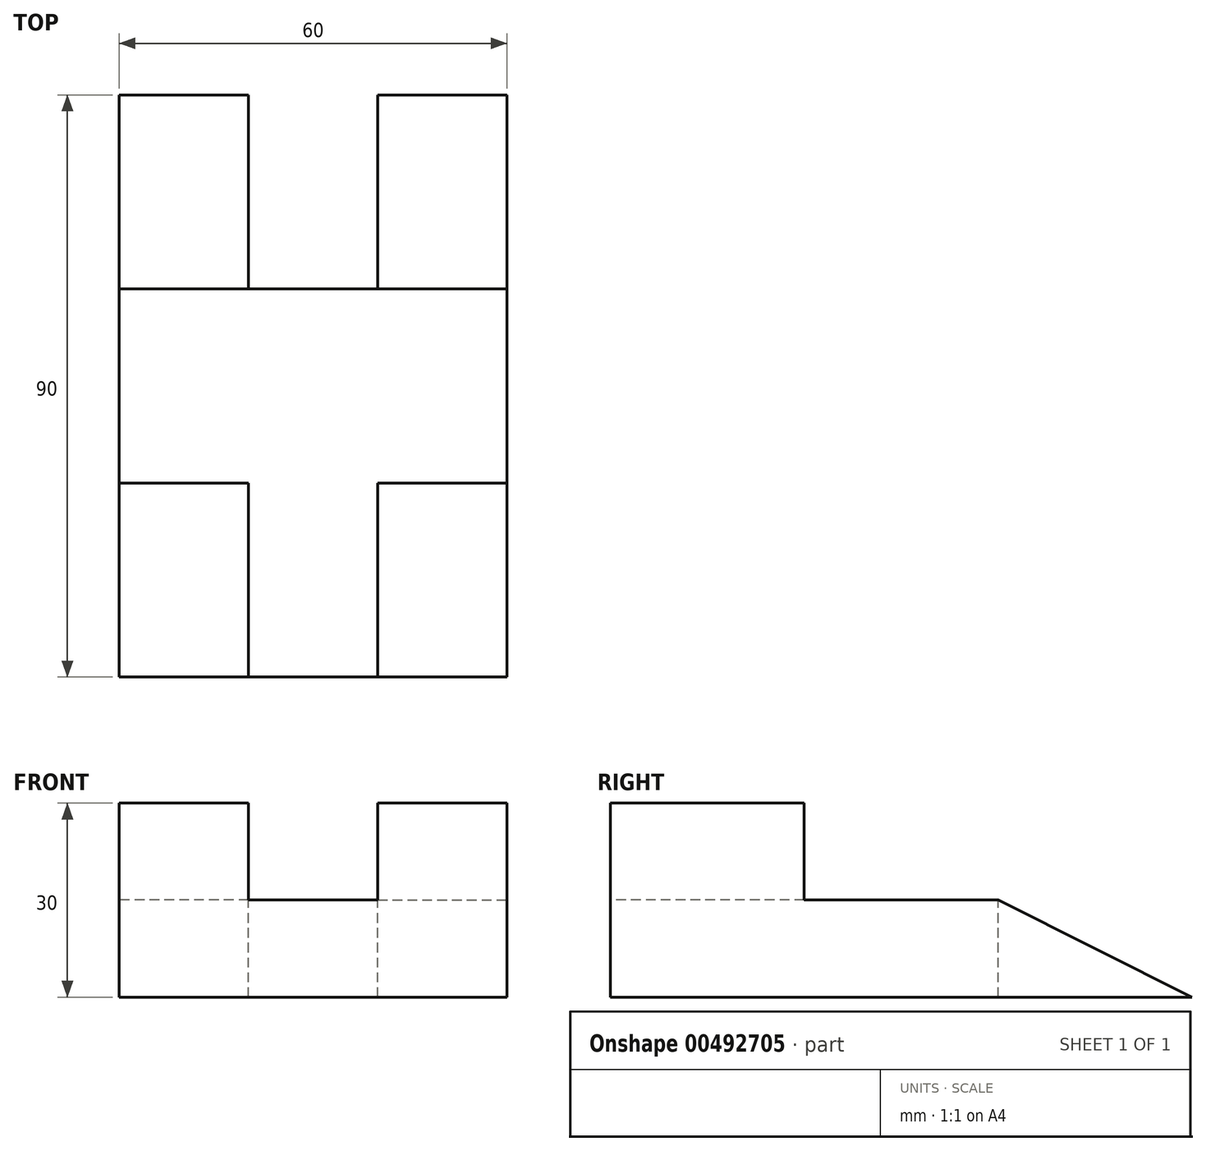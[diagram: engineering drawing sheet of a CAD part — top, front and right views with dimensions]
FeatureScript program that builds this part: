
annotation { "Feature Type Name" : "Feature", "Feature Type Description" : "" }
export const myFeature = defineFeature(function(context is Context, id is Id, definition is map)
    precondition{}
    {
        {
            var Q0;
            Q0=qCreatedBy(makeId("Top.planeOp"),FACE);
            var sketch = newSketch(context, id + "F0", { "sketchPlane" : qUnion([Q0])});
            skPoint(sketch, "E0", {"position": v(-59.64, 62.98) * mm});
            skPoint(sketch, "E1", {"position": v(0.36, 62.98) * mm});
            skPoint(sketch, "E2", {"position": v(0.36, -27.02) * mm});
            skPoint(sketch, "E3", {"position": v(-59.64, -27.02) * mm});
            skLineSegment(sketch, "E4", {"start": v(-59.64, 62.98) * mm, "end": v(-59.64, -27.02) * mm});
            skLineSegment(sketch, "E5", {"start": v(-59.64, -27.02) * mm, "end": v(0.36, -27.02) * mm});
            skLineSegment(sketch, "E6", {"start": v(-59.64, 62.98) * mm, "end": v(0.36, 62.98) * mm});
            skLineSegment(sketch, "E7", {"start": v(0.36, 62.98) * mm, "end": v(0.36, -27.02) * mm});
            skSolve(sketch);
        }
        {
            var Q0;
            Q0=makeQuery(id+"F0.imprint","IMPRINT",FACE,{"disambiguationData":[TD([[makeQuery(id+"F0.imprint","IMPRINT",EDGE,{"derivedFrom":sQuery(id+"F0.wireOp",EDGE,"E4")}),1.0]])]});
            extrude(context, id + "F1", {"entities" : qUnion([Q0]), "depth" : 15 * mm});
        }
        {
            var Q0;
            Q0=makeQuery(id+"F1.opExtrude","CAP_FACE",FACE,{"disambiguationData":[OSD([sQuery(id+"F0.wireOp",EDGE,"E4"),sQuery(id+"F0.wireOp",EDGE,"E5"),sQuery(id+"F0.wireOp",EDGE,"E6"),sQuery(id+"F0.wireOp",EDGE,"E7")])],"isStart":false});
            var sketch = newSketch(context, id + "F2", { "sketchPlane" : qUnion([Q0])});
            skLineSegment(sketch, "E8.bottom", {"start": v(-59.64, 2.98) * mm, "end": v(-39.64, 2.98) * mm});
            skLineSegment(sketch, "E8.top", {"start": v(-59.64, -27.02) * mm, "end": v(-39.64, -27.02) * mm});
            skLineSegment(sketch, "E8.left", {"start": v(-59.64, 2.98) * mm, "end": v(-59.64, -27.02) * mm});
            skLineSegment(sketch, "E8.right", {"start": v(-39.64, 2.98) * mm, "end": v(-39.64, -27.02) * mm});
            skLineSegment(sketch, "E9.bottom", {"start": v(-19.64, 2.98) * mm, "end": v(0.36, 2.98) * mm});
            skLineSegment(sketch, "E9.top", {"start": v(-19.64, -27.02) * mm, "end": v(0.36, -27.02) * mm});
            skLineSegment(sketch, "E9.left", {"start": v(-19.64, 2.98) * mm, "end": v(-19.64, -27.02) * mm});
            skLineSegment(sketch, "E9.right", {"start": v(0.36, 2.98) * mm, "end": v(0.36, -27.02) * mm});
            skSolve(sketch);
        }
        {
            var Q0;
            Q0 = qSketchRegion(id + "F2", true);
            extrude(context, id + "F3", {"entities" : qUnion([Q0]), "operationType" : NewBodyOperationType.ADD, "depth" : 15 * mm});
        }
        {
            var Q0;
            Q0=makeQuery(id+"F1.opExtrude","CAP_FACE",FACE,{"disambiguationData":[OSD([sQuery(id+"F0.wireOp",EDGE,"E4"),sQuery(id+"F0.wireOp",EDGE,"E5"),sQuery(id+"F0.wireOp",EDGE,"E6"),sQuery(id+"F0.wireOp",EDGE,"E7")])],"isStart":false});
            var sketch = newSketch(context, id + "F4", { "sketchPlane" : qUnion([Q0])});
            skLineSegment(sketch, "E10.bottom", {"start": v(-59.64, 62.98) * mm, "end": v(-39.64, 62.98) * mm});
            skLineSegment(sketch, "E10.top", {"start": v(-59.64, 32.98) * mm, "end": v(-39.64, 32.98) * mm});
            skLineSegment(sketch, "E10.left", {"start": v(-59.64, 62.98) * mm, "end": v(-59.64, 32.98) * mm});
            skLineSegment(sketch, "E10.right", {"start": v(-39.64, 62.98) * mm, "end": v(-39.64, 32.98) * mm});
            skLineSegment(sketch, "E11.bottom", {"start": v(0.36, 62.98) * mm, "end": v(-19.64, 62.98) * mm});
            skLineSegment(sketch, "E11.top", {"start": v(0.36, 32.98) * mm, "end": v(-19.64, 32.98) * mm});
            skLineSegment(sketch, "E11.left", {"start": v(0.36, 62.98) * mm, "end": v(0.36, 32.98) * mm});
            skLineSegment(sketch, "E11.right", {"start": v(-19.64, 62.98) * mm, "end": v(-19.64, 32.98) * mm});
            skSolve(sketch);
        }
        {
            var Q0;
            Q0=makeQuery(id+"F1.opExtrude","CAP_FACE",FACE,{"disambiguationData":[OSD([sQuery(id+"F0.wireOp",EDGE,"E4"),sQuery(id+"F0.wireOp",EDGE,"E5"),sQuery(id+"F0.wireOp",EDGE,"E6"),sQuery(id+"F0.wireOp",EDGE,"E7")])],"isStart":false});
            var sketch = newSketch(context, id + "F5", { "sketchPlane" : qUnion([Q0])});
            skLineSegment(sketch, "E12.bottom", {"start": v(-39.64, 62.98) * mm, "end": v(-19.64, 62.98) * mm});
            skLineSegment(sketch, "E12.top", {"start": v(-39.64, 32.98) * mm, "end": v(-19.64, 32.98) * mm});
            skLineSegment(sketch, "E12.left", {"start": v(-39.64, 62.98) * mm, "end": v(-39.64, 32.98) * mm});
            skLineSegment(sketch, "E12.right", {"start": v(-19.64, 62.98) * mm, "end": v(-19.64, 32.98) * mm});
            skSolve(sketch);
        }
        {
            var Q0;
            Q0 = qSketchRegion(id + "F5", true);
            extrude(context, id + "F6", {"entities" : qUnion([Q0]), "operationType" : NewBodyOperationType.REMOVE, "oppositeDirection" : true, "depth" : 15 * mm});
        }
        {
            var Q0;
            Q0=makeQuery(id+"F3.boolean.opBoolean","MERGE",FACE,{"derivedFrom":[makeQuery(id+"F1.opExtrude","SWEPT_FACE",FACE,{"disambiguationData":[OSD([sQuery(id+"F0.wireOp",EDGE,"E4")])]}),makeQuery(id+"F3.opExtrude","SWEPT_FACE",FACE,{"disambiguationData":[OSD([sQuery(id+"F2.wireOp",EDGE,"E8.left")])]})]});
            var sketch = newSketch(context, id + "F7", { "sketchPlane" : qUnion([Q0])});
            skLineSegment(sketch, "E13", {"start": v(-62.98, 0) * mm, "end": v(-32.98, 15) * mm});
            skLineSegment(sketch, "E14", {"start": v(-32.98, 15) * mm, "end": v(-60.44, 15) * mm});
            skLineSegment(sketch, "E15", {"start": v(-62.98, 0) * mm, "end": v(-62.98, 15) * mm});
            skLineSegment(sketch, "E16", {"start": v(-62.98, 15) * mm, "end": v(-32.98, 15) * mm});
            skSolve(sketch);
        }
        {
            var Q0;
            {var subQ0=sQuery(id+"F7.wireOp",EDGE,"E13");Q0=makeQuery(id+"F7.imprint","IMPRINT",FACE,{"disambiguationData":[TD([[makeQuery(id+"F7.imprint","IMPRINT",EDGE,{"derivedFrom":subQ0}),1.0]])]});}
            extrude(context, id + "F8", {"entities" : qUnion([Q0]), "operationType" : NewBodyOperationType.REMOVE, "oppositeDirection" : true, "depth" : 25 * mm});
        }
        {
            var Q0;
            Q0=makeQuery(id+"F3.boolean.opBoolean","MERGE",FACE,{"derivedFrom":[makeQuery(id+"F1.opExtrude","SWEPT_FACE",FACE,{"disambiguationData":[OSD([sQuery(id+"F0.wireOp",EDGE,"E7")])]}),makeQuery(id+"F3.opExtrude","SWEPT_FACE",FACE,{"disambiguationData":[OSD([sQuery(id+"F2.wireOp",EDGE,"E9.right")])]})]});
            var sketch = newSketch(context, id + "F9", { "sketchPlane" : qUnion([Q0])});
            skLineSegment(sketch, "E17", {"start": v(62.98, 0) * mm, "end": v(32.98, 15) * mm});
            skLineSegment(sketch, "E18", {"start": v(62.98, 15) * mm, "end": v(62.98, 0) * mm});
            skLineSegment(sketch, "E19", {"start": v(32.98, 15) * mm, "end": v(62.98, 15) * mm});
            skSolve(sketch);
        }
        {
            var Q0;
            Q0=makeQuery(id+"F9.imprint","IMPRINT",FACE,{"disambiguationData":[TD([[makeQuery(id+"F9.imprint","IMPRINT",EDGE,{"derivedFrom":sQuery(id+"F9.wireOp",EDGE,"E17")}),-1.0]])]});
            extrude(context, id + "F10", {"entities" : qUnion([Q0]), "operationType" : NewBodyOperationType.REMOVE, "oppositeDirection" : true, "depth" : 25 * mm});
        }
    });
